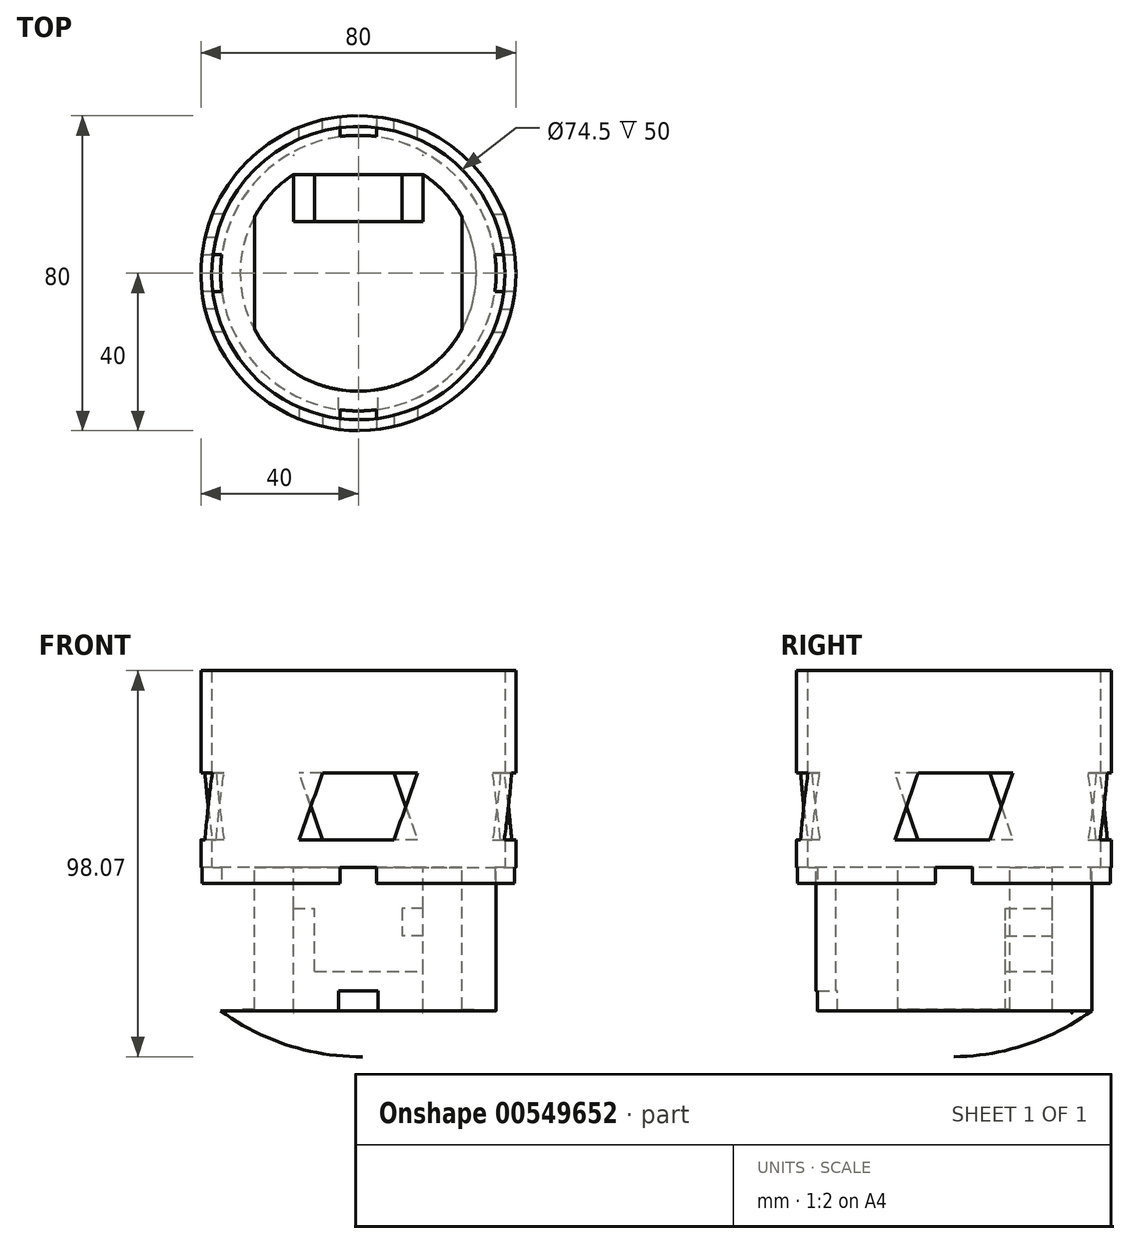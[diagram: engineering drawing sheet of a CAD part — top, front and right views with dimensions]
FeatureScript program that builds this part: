
annotation { "Feature Type Name" : "Feature", "Feature Type Description" : "" }
export const myFeature = defineFeature(function(context is Context, id is Id, definition is map)
    precondition{}
    {
        {
            var Q0;
            Q0=qCreatedBy(makeId("Top.planeOp"),FACE);
            var sketch = newSketch(context, id + "F0", { "sketchPlane" : qUnion([Q0])});
            skCircle(sketch, "E0", {"center": v(0, 0) * mm, "radius": 35 * mm});
            skCircle(sketch, "E1", {"center": v(0, 0) * mm, "radius": 30 * mm});
            skSolve(sketch);
        }
        {
            var Q0;
            Q0=makeQuery(id+"F0.imprint","IMPRINT",FACE,{"disambiguationData":[TD([[makeQuery(id+"F0.imprint","IMPRINT",EDGE,{"derivedFrom":sQuery(id+"F0.wireOp",EDGE,"E0")}),1.0]])]});
            extrude(context, id + "F1", {"entities" : qUnion([Q0]), "oppositeDirection" : true, "depth" : 10 * mm, "offsetDistance" : 25 * mm});
        }
        {
            var Q0;
            Q0=qCreatedBy(makeId("Top.planeOp"),FACE);
            var sketch = newSketch(context, id + "F2", { "sketchPlane" : qUnion([Q0])});
            skLineSegment(sketch, "E2.bottom", {"start": v(4.67, 54) * mm, "end": v(-4.68, 54) * mm});
            skLineSegment(sketch, "E2.top", {"start": v(4.68, 34) * mm, "end": v(-4.67, 34) * mm});
            skLineSegment(sketch, "E2.left", {"start": v(4.68, 54) * mm, "end": v(4.68, 34) * mm});
            skLineSegment(sketch, "E2.right", {"start": v(-4.67, 54) * mm, "end": v(-4.67, 34) * mm});
            skPoint(sketch, "E2.middle", {"position": v(0, 44) * mm});
            skSolve(sketch);
        }
        {
            var Q0;
            Q0=qSketchRegion(id+"F2",true);
            extrude(context, id + "F3", {"entities" : qUnion([Q0]), "operationType" : NewBodyOperationType.ADD, "oppositeDirection" : true, "depth" : 10 * mm, "offsetDistance" : 25 * mm});
        }
        {
            var Q0;
            Q0=qCreatedBy(makeId("Right.planeOp"),FACE);
            var sketch = newSketch(context, id + "F4", { "sketchPlane" : qUnion([Q0])});
            skLineSegment(sketch, "E3", {"start": v(0, 0) * mm, "end": v(0, -40) * mm});
            skSolve(sketch);
        }
        {
            var Q0;
            Q0=makeQuery(id+"F1.opExtrude","CAP_FACE",FACE,{"disambiguationData":[OSD([sQuery(id+"F0.wireOp",EDGE,"E0"),sQuery(id+"F0.wireOp",EDGE,"E1")])],"isStart":false});
            var sketch = newSketch(context, id + "F5", { "sketchPlane" : qUnion([Q0])});
            skCircle(sketch, "E4", {"center": v(0, 0) * mm, "radius": 30 * mm});
            skCircle(sketch, "E5", {"center": v(0, 0) * mm, "radius": 35 * mm});
            skSolve(sketch);
        }
        {
            var Q0;
            Q0=qSketchRegion(id+"F5",true);
            extrude(context, id + "F6", {"entities" : qUnion([Q0]), "depth" : 26.4 * mm, "offsetDistance" : 25 * mm});
        }
        {
            var Q0;
            Q0=qCreatedBy(makeId("Right.planeOp"),FACE);
            var sketch = newSketch(context, id + "F7", { "sketchPlane" : qUnion([Q0])});
            skLineSegment(sketch, "E6", {"start": v(0, 43.23) * mm, "end": v(0, 10.88) * mm});
            skSolve(sketch);
        }
        {
            var Q0;
            Q0=makeQuery(id+"F1.opExtrude","SWEPT_BODY",BODY,{"disambiguationData":[OSD([sQuery(id+"F0.wireOp",EDGE,"E0"),sQuery(id+"F0.wireOp",EDGE,"E1")])]});
            var Q1;
            Q1=sQuery(id+"F7.wireOp",EDGE,"E6");
            circularPattern(context, id + "F8", {"entities" : qUnion([Q0]), "axis" : qUnion([Q1]), "angle" : 360 * degree, "instanceCount" : 4, "equalSpace" : true});
        }
        {
            var Q0;
            Q0=qCreatedBy(makeId("Right.planeOp"),FACE);
            var sketch = newSketch(context, id + "F9", { "sketchPlane" : qUnion([Q0])});
            skLineSegment(sketch, "E7", {"start": v(0, -36.4) * mm, "end": v(0, -48.07) * mm});
            skLineSegment(sketch, "E8", {"start": v(0, -36.4) * mm, "end": v(-35, -36.4) * mm});
            skArc(sketch, "E9", {"start": v(-35, -36.4) * mm, "mid": v(-18.42, -44.99) * mm, "end": v(0, -48.07) * mm});
            skSolve(sketch);
        }
        {
            var Q0;
            Q0=qSketchRegion(id+"F9",true);
            var Q1;
            Q1=sQuery(id+"F7.wireOp",EDGE,"E6");
            revolve(context, id + "F10", {"operationType" : NewBodyOperationType.ADD, "entities" : qUnion([Q0]), "axis" : qUnion([Q1]), "revolveType" : RevolveType.FULL});
        }
        {
            var Q0;
            Q0=qCreatedBy(makeId("Top.planeOp"),FACE);
            var sketch = newSketch(context, id + "F11", { "sketchPlane" : qUnion([Q0])});
            skLineSegment(sketch, "E10.bottom", {"start": v(16.5, 25.05) * mm, "end": v(-16.5, 25.05) * mm});
            skLineSegment(sketch, "E10.top", {"start": v(16.5, 30) * mm, "end": v(-16.5, 30) * mm});
            skLineSegment(sketch, "E10.left", {"start": v(16.5, 25.05) * mm, "end": v(16.5, 30) * mm});
            skLineSegment(sketch, "E10.right", {"start": v(-16.5, 25.05) * mm, "end": v(-16.5, 30) * mm});
            skPoint(sketch, "E10.middle", {"position": v(0, 27.53) * mm});
            skSolve(sketch);
        }
        {
            var Q0;
            Q0=makeQuery(id+"F1.opExtrude","SWEPT_BODY",BODY,{"disambiguationData":[OSD([sQuery(id+"F0.wireOp",EDGE,"E0"),sQuery(id+"F0.wireOp",EDGE,"E1")])]});
            var Q1;
            Q1=makeQuery(id+"F6.opExtrude","SWEPT_BODY",BODY,{"disambiguationData":[OSD([sQuery(id+"F5.wireOp",EDGE,"E4"),sQuery(id+"F5.wireOp",EDGE,"E5")])]});
            var Q2;
            Q2=makeQuery(id+"F8.opPattern","COPY",BODY,{"derivedFrom":makeQuery(id+"F1.opExtrude","SWEPT_BODY",BODY,{"disambiguationData":[OSD([sQuery(id+"F0.wireOp",EDGE,"E0"),sQuery(id+"F0.wireOp",EDGE,"E1")])]}),"instanceName":"2"});
            var Q3;
            Q3=makeQuery(id+"F8.opPattern","COPY",BODY,{"derivedFrom":makeQuery(id+"F1.opExtrude","SWEPT_BODY",BODY,{"disambiguationData":[OSD([sQuery(id+"F0.wireOp",EDGE,"E0"),sQuery(id+"F0.wireOp",EDGE,"E1")])]}),"instanceName":"3"});
            var Q4;
            Q4=makeQuery(id+"F40aK8SqE4txYRV_3.opPattern","COPY",BODY,{"derivedFrom":makeQuery(id+"FKwpcLcn6bH6iQZ_2.opRevolve","SWEPT_BODY",BODY,{"disambiguationData":[OSD([sQuery(id+"FD4HdzIvPUUwVay_2.wireOp",EDGE,"a1goFWV3-hmGV-yWYP-BMxk-jAgMXw5Fhpe8"),sQuery(id+"FD4HdzIvPUUwVay_2.wireOp",EDGE,"Fw7PGfqN-QWwp-sSqB-PI52-uVMqbdzyiW2G"),sQuery(id+"FD4HdzIvPUUwVay_2.wireOp",EDGE,"nihQI9GH-8jKx-viQP-mQeq-4tLKAg00kZ77"),sQuery(id+"FD4HdzIvPUUwVay_2.wireOp",EDGE,"Pyl0iUsN-Orhq-JqrC-4vEJ-9OXzgTH1srMD")])]}),"instanceName":"1"});
            booleanBodies(context, id + "F12", {"operationType" : BooleanOperationType.UNION, "tools" : qUnion([Q0, Q1, Q2, Q3, Q4])});
        }
        {
            var Q0;
            Q0=makeQuery(id+"F1.opExtrude","SWEPT_BODY",BODY,{"disambiguationData":[OSD([sQuery(id+"F0.wireOp",EDGE,"E0"),sQuery(id+"F0.wireOp",EDGE,"E1")])]});
            var Q1;
            Q1=makeQuery(id+"F8.opPattern","COPY",BODY,{"derivedFrom":makeQuery(id+"F1.opExtrude","SWEPT_BODY",BODY,{"disambiguationData":[OSD([sQuery(id+"F0.wireOp",EDGE,"E0"),sQuery(id+"F0.wireOp",EDGE,"E1")])]}),"instanceName":"1"});
            var Q2;
            Q2=makeQuery(id+"FKwpcLcn6bH6iQZ_2.opRevolve","SWEPT_BODY",BODY,{"disambiguationData":[OSD([sQuery(id+"FD4HdzIvPUUwVay_2.wireOp",EDGE,"a1goFWV3-hmGV-yWYP-BMxk-jAgMXw5Fhpe8"),sQuery(id+"FD4HdzIvPUUwVay_2.wireOp",EDGE,"Fw7PGfqN-QWwp-sSqB-PI52-uVMqbdzyiW2G"),sQuery(id+"FD4HdzIvPUUwVay_2.wireOp",EDGE,"nihQI9GH-8jKx-viQP-mQeq-4tLKAg00kZ77"),sQuery(id+"FD4HdzIvPUUwVay_2.wireOp",EDGE,"Pyl0iUsN-Orhq-JqrC-4vEJ-9OXzgTH1srMD")])]});
            var Q3;
            Q3=makeQuery(id+"F40aK8SqE4txYRV_3.opPattern","COPY",BODY,{"derivedFrom":makeQuery(id+"FKwpcLcn6bH6iQZ_2.opRevolve","SWEPT_BODY",BODY,{"disambiguationData":[OSD([sQuery(id+"FD4HdzIvPUUwVay_2.wireOp",EDGE,"a1goFWV3-hmGV-yWYP-BMxk-jAgMXw5Fhpe8"),sQuery(id+"FD4HdzIvPUUwVay_2.wireOp",EDGE,"Fw7PGfqN-QWwp-sSqB-PI52-uVMqbdzyiW2G"),sQuery(id+"FD4HdzIvPUUwVay_2.wireOp",EDGE,"nihQI9GH-8jKx-viQP-mQeq-4tLKAg00kZ77"),sQuery(id+"FD4HdzIvPUUwVay_2.wireOp",EDGE,"Pyl0iUsN-Orhq-JqrC-4vEJ-9OXzgTH1srMD")])]}),"instanceName":"2"});
            var Q4;
            Q4=makeQuery(id+"F40aK8SqE4txYRV_3.opPattern","COPY",BODY,{"derivedFrom":makeQuery(id+"FKwpcLcn6bH6iQZ_2.opRevolve","SWEPT_BODY",BODY,{"disambiguationData":[OSD([sQuery(id+"FD4HdzIvPUUwVay_2.wireOp",EDGE,"a1goFWV3-hmGV-yWYP-BMxk-jAgMXw5Fhpe8"),sQuery(id+"FD4HdzIvPUUwVay_2.wireOp",EDGE,"Fw7PGfqN-QWwp-sSqB-PI52-uVMqbdzyiW2G"),sQuery(id+"FD4HdzIvPUUwVay_2.wireOp",EDGE,"nihQI9GH-8jKx-viQP-mQeq-4tLKAg00kZ77"),sQuery(id+"FD4HdzIvPUUwVay_2.wireOp",EDGE,"Pyl0iUsN-Orhq-JqrC-4vEJ-9OXzgTH1srMD")])]}),"instanceName":"3"});
            var Q5;
            Q5=makeQuery(id+"FgH07LaCN1YdpZV_3.opExtrude","SWEPT_BODY",BODY,{"disambiguationData":[OSD([sQuery(id+"FR34k6RjlDwe5vP_3.wireOp",EDGE,"LmRDcWpp-awj7-NGUQ-v67H-xGxEU0ThPCFp"),sQuery(id+"FR34k6RjlDwe5vP_3.wireOp",EDGE,"yXPaf9AL-SZNH-Mc4A-USQs-dOwJlW72xKXk"),sQuery(id+"FR34k6RjlDwe5vP_3.wireOp",EDGE,"sUruhic9-czyD-tmxL-6hvL-q4A46Xcr3Ddl"),sQuery(id+"FR34k6RjlDwe5vP_3.wireOp",EDGE,"kMsjgBrX-0vqh-hQ1Y-Rj0W-wmr9ZrnzLnDL")])]});
            var Q6;
            Q6=makeQuery(id+"FhvvMPg10EEFssR_4.opPattern","COPY",BODY,{"derivedFrom":makeQuery(id+"FgH07LaCN1YdpZV_3.opExtrude","SWEPT_BODY",BODY,{"disambiguationData":[OSD([sQuery(id+"FR34k6RjlDwe5vP_3.wireOp",EDGE,"LmRDcWpp-awj7-NGUQ-v67H-xGxEU0ThPCFp"),sQuery(id+"FR34k6RjlDwe5vP_3.wireOp",EDGE,"yXPaf9AL-SZNH-Mc4A-USQs-dOwJlW72xKXk"),sQuery(id+"FR34k6RjlDwe5vP_3.wireOp",EDGE,"sUruhic9-czyD-tmxL-6hvL-q4A46Xcr3Ddl"),sQuery(id+"FR34k6RjlDwe5vP_3.wireOp",EDGE,"kMsjgBrX-0vqh-hQ1Y-Rj0W-wmr9ZrnzLnDL")])]}),"instanceName":"1"});
            var Q7;
            Q7=makeQuery(id+"F8pSuF8Lx7vEzgG_4.opExtrude","SWEPT_BODY",BODY,{"disambiguationData":[OSD([sQuery(id+"F11.wireOp",EDGE,"E10.bottom"),sQuery(id+"F11.wireOp",EDGE,"E10.top"),sQuery(id+"F11.wireOp",EDGE,"E10.left"),sQuery(id+"F11.wireOp",EDGE,"E10.right")])]});
            var Q8;
            Q8=makeQuery(id+"FjD0aHrHDqX2kuE_5.opExtrude","SWEPT_BODY",BODY,{"disambiguationData":[OSD([sQuery(id+"FjwMsoveauJ2MpE_5.wireOp",EDGE,"X3daKeJd-6pMJ-jMlG-joWg-jZjprT1OWdNl.bottom"),sQuery(id+"FjwMsoveauJ2MpE_5.wireOp",EDGE,"X3daKeJd-6pMJ-jMlG-joWg-jZjprT1OWdNl.top"),sQuery(id+"FjwMsoveauJ2MpE_5.wireOp",EDGE,"X3daKeJd-6pMJ-jMlG-joWg-jZjprT1OWdNl.left"),sQuery(id+"FjwMsoveauJ2MpE_5.wireOp",EDGE,"X3daKeJd-6pMJ-jMlG-joWg-jZjprT1OWdNl.right")])]});
            var Q9;
            Q9=makeQuery(id+"FjD0aHrHDqX2kuE_5.opExtrude","SWEPT_BODY",BODY,{"disambiguationData":[OSD([sQuery(id+"FjwMsoveauJ2MpE_5.wireOp",EDGE,"aEOO42Y5-tFNn-AOk7-4746-zKCDvE4CHbXH.bottom"),sQuery(id+"FjwMsoveauJ2MpE_5.wireOp",EDGE,"aEOO42Y5-tFNn-AOk7-4746-zKCDvE4CHbXH.top"),sQuery(id+"FjwMsoveauJ2MpE_5.wireOp",EDGE,"aEOO42Y5-tFNn-AOk7-4746-zKCDvE4CHbXH.left"),sQuery(id+"FjwMsoveauJ2MpE_5.wireOp",EDGE,"aEOO42Y5-tFNn-AOk7-4746-zKCDvE4CHbXH.right"),sQuery(id+"FjwMsoveauJ2MpE_5.wireOp",EDGE,"ugEVnK5k-7QH2-G8G2-oESj-ZDwBd6VaRQGP.top"),sQuery(id+"FjwMsoveauJ2MpE_5.wireOp",EDGE,"ugEVnK5k-7QH2-G8G2-oESj-ZDwBd6VaRQGP.left"),sQuery(id+"FjwMsoveauJ2MpE_5.wireOp",EDGE,"ugEVnK5k-7QH2-G8G2-oESj-ZDwBd6VaRQGP.right")])]});
            booleanBodies(context, id + "F13", {"operationType" : BooleanOperationType.UNION, "tools" : qUnion([Q0, Q1, Q2, Q3, Q4, Q5, Q6, Q7, Q8, Q9])});
        }
        {
            var Q0;
            Q0=qSketchRegion(id+"F11",true);
            extrude(context, id + "F14", {"entities" : qUnion([Q0]), "operationType" : NewBodyOperationType.ADD, "oppositeDirection" : true, "depth" : 37 * mm, "offsetDistance" : 25 * mm});
        }
        {
            var Q0;
            Q0=makeQuery(id+"F14.opExtrude","SWEPT_FACE",FACE,{"disambiguationData":[OSD([sQuery(id+"F11.wireOp",EDGE,"E10.bottom")])]});
            var sketch = newSketch(context, id + "F15", { "sketchPlane" : qUnion([Q0])});
            skLineSegment(sketch, "E11.bottom", {"start": v(-16.5, -36.4) * mm, "end": v(16.5, -36.4) * mm});
            skLineSegment(sketch, "E11.top", {"start": v(-16.5, -26.4) * mm, "end": v(16.5, -26.4) * mm});
            skLineSegment(sketch, "E11.left", {"start": v(-16.5, -36.4) * mm, "end": v(-16.5, -26.4) * mm});
            skLineSegment(sketch, "E11.right", {"start": v(16.5, -36.4) * mm, "end": v(16.5, -26.4) * mm});
            skLineSegment(sketch, "E12.bottom", {"start": v(-16.5, -26.4) * mm, "end": v(-11.1, -26.4) * mm});
            skLineSegment(sketch, "E12.top", {"start": v(-16.5, -10.4) * mm, "end": v(-11.1, -10.4) * mm});
            skLineSegment(sketch, "E12.left", {"start": v(-16.5, -26.4) * mm, "end": v(-16.5, -10.4) * mm});
            skLineSegment(sketch, "E12.right", {"start": v(-11.1, -26.4) * mm, "end": v(-11.1, -10.4) * mm});
            skLineSegment(sketch, "E13.bottom", {"start": v(16.5, -10.4) * mm, "end": v(11.1, -10.4) * mm});
            skLineSegment(sketch, "E13.top", {"start": v(16.5, -17.4) * mm, "end": v(11.1, -17.4) * mm});
            skLineSegment(sketch, "E13.left", {"start": v(16.5, -10.4) * mm, "end": v(16.5, -17.4) * mm});
            skLineSegment(sketch, "E13.right", {"start": v(11.1, -10.4) * mm, "end": v(11.1, -17.4) * mm});
            skSolve(sketch);
        }
        {
            var Q0;
            Q0=qSketchRegion(id+"F15",true);
            extrude(context, id + "F16", {"entities" : qUnion([Q0]), "operationType" : NewBodyOperationType.ADD, "depth" : 12 * mm, "offsetDistance" : 25 * mm});
        }
        {
            var Q0;
            {var subQ0=makeQuery(id+"F3.boolean.opBoolean","MERGE",FACE,{"derivedFrom":[makeQuery(id+"F1.opExtrude","CAP_FACE",FACE,{"disambiguationData":[OSD([sQuery(id+"F0.wireOp",EDGE,"E0"),sQuery(id+"F0.wireOp",EDGE,"E1")])],"isStart":true}),makeQuery(id+"F3.opExtrude","CAP_FACE",FACE,{"disambiguationData":[OSD([sQuery(id+"F2.wireOp",EDGE,"E2.bottom"),sQuery(id+"F2.wireOp",EDGE,"E2.top"),sQuery(id+"F2.wireOp",EDGE,"E2.left"),sQuery(id+"F2.wireOp",EDGE,"E2.right")])],"isStart":true})]});Q0=makeQuery(id+"F14.boolean.opBoolean","MERGE",FACE,{"derivedFrom":[makeQuery(id+"F13.opBoolean","MERGE",FACE,{"derivedFrom":[makeQuery(id+"F8.opPattern","COPY",FACE,{"derivedFrom":subQ0,"instanceName":"1"}),makeQuery(id+"F12.opBoolean","MERGE",FACE,{"derivedFrom":[subQ0,makeQuery(id+"F8.opPattern","COPY",FACE,{"derivedFrom":subQ0,"instanceName":"2"}),makeQuery(id+"F8.opPattern","COPY",FACE,{"derivedFrom":subQ0,"instanceName":"3"})]})]}),makeQuery(id+"F14.opExtrude","CAP_FACE",FACE,{"disambiguationData":[OSD([sQuery(id+"F11.wireOp",EDGE,"E10.bottom"),sQuery(id+"F11.wireOp",EDGE,"E10.top"),sQuery(id+"F11.wireOp",EDGE,"E10.left"),sQuery(id+"F11.wireOp",EDGE,"E10.right")])],"isStart":true})]});}
            var sketch = newSketch(context, id + "F17", { "sketchPlane" : qUnion([Q0])});
            skLineSegment(sketch, "E14.bottom", {"start": v(-31.49, 14.23) * mm, "end": v(-26.4, 14.23) * mm});
            skLineSegment(sketch, "E14.top", {"start": v(-31.49, -14.23) * mm, "end": v(-26.4, -14.23) * mm});
            skLineSegment(sketch, "E14.left", {"start": v(-31.49, 14.23) * mm, "end": v(-31.49, -14.23) * mm});
            skLineSegment(sketch, "E14.right", {"start": v(-26.4, 14.23) * mm, "end": v(-26.4, -14.23) * mm});
            skLineSegment(sketch, "E15", {"start": v(0, 0) * mm, "end": v(0, -11.57) * mm, "construction": true});
            skLineSegment(sketch, "E16.MirrorCS", {"start": v(26.4, 14.23) * mm, "end": v(26.4, -14.23) * mm});
            skLineSegment(sketch, "E17.MirrorCS", {"start": v(31.49, 14.23) * mm, "end": v(31.49, -14.23) * mm});
            skLineSegment(sketch, "E18.MirrorCS", {"start": v(31.49, 14.23) * mm, "end": v(26.4, 14.23) * mm});
            skLineSegment(sketch, "E19.MirrorCS", {"start": v(31.49, -14.23) * mm, "end": v(26.4, -14.23) * mm});
            skSolve(sketch);
        }
        {
            var Q0;
            Q0=qSketchRegion(id+"F17",true);
            extrude(context, id + "F18", {"entities" : qUnion([Q0]), "operationType" : NewBodyOperationType.ADD, "oppositeDirection" : true, "depth" : 36 * mm, "offsetDistance" : 25 * mm});
        }
        {
            var Q0;
            Q0=makeQuery(id+"F16.opExtrude","CAP_FACE",FACE,{"disambiguationData":[OSD([sQuery(id+"F15.wireOp",EDGE,"E11.bottom"),sQuery(id+"F15.wireOp",EDGE,"E11.top"),sQuery(id+"F15.wireOp",EDGE,"E11.left"),sQuery(id+"F15.wireOp",EDGE,"E11.right"),sQuery(id+"F15.wireOp",EDGE,"E12.top"),sQuery(id+"F15.wireOp",EDGE,"E12.left"),sQuery(id+"F15.wireOp",EDGE,"E12.right")])],"isStart":false});
            var sketch = newSketch(context, id + "F19", { "sketchPlane" : qUnion([Q0])});
            skLineSegment(sketch, "E20.bottom", {"start": v(5, -36.4) * mm, "end": v(-5, -36.4) * mm});
            skLineSegment(sketch, "E20.top", {"start": v(5, -31.4) * mm, "end": v(-5, -31.4) * mm});
            skLineSegment(sketch, "E20.left", {"start": v(5, -36.4) * mm, "end": v(5, -31.4) * mm});
            skLineSegment(sketch, "E20.right", {"start": v(-5, -36.4) * mm, "end": v(-5, -31.4) * mm});
            skPoint(sketch, "E20.middle", {"position": v(0, -33.9) * mm});
            skSolve(sketch);
        }
        {
            var Q0;
            Q0=qSketchRegion(id+"F19",true);
            extrude(context, id + "F20", {"entities" : qUnion([Q0]), "operationType" : NewBodyOperationType.REMOVE, "depth" : 54.2 * mm, "offsetDistance" : 25 * mm});
        }
        {
            var Q0;
            {var subQ0=makeQuery(id+"F3.boolean.opBoolean","MERGE",FACE,{"derivedFrom":[makeQuery(id+"F1.opExtrude","CAP_FACE",FACE,{"disambiguationData":[OSD([sQuery(id+"F0.wireOp",EDGE,"E0"),sQuery(id+"F0.wireOp",EDGE,"E1")])],"isStart":true}),makeQuery(id+"F3.opExtrude","CAP_FACE",FACE,{"disambiguationData":[OSD([sQuery(id+"F2.wireOp",EDGE,"E2.bottom"),sQuery(id+"F2.wireOp",EDGE,"E2.top"),sQuery(id+"F2.wireOp",EDGE,"E2.left"),sQuery(id+"F2.wireOp",EDGE,"E2.right")])],"isStart":true})]});Q0=makeQuery(id+"F18.boolean.opBoolean","MERGE",FACE,{"derivedFrom":[makeQuery(id+"F14.boolean.opBoolean","MERGE",FACE,{"derivedFrom":[makeQuery(id+"F13.opBoolean","MERGE",FACE,{"derivedFrom":[makeQuery(id+"F8.opPattern","COPY",FACE,{"derivedFrom":subQ0,"instanceName":"1"}),makeQuery(id+"F12.opBoolean","MERGE",FACE,{"derivedFrom":[subQ0,makeQuery(id+"F8.opPattern","COPY",FACE,{"derivedFrom":subQ0,"instanceName":"2"}),makeQuery(id+"F8.opPattern","COPY",FACE,{"derivedFrom":subQ0,"instanceName":"3"})]})]}),makeQuery(id+"F14.opExtrude","CAP_FACE",FACE,{"disambiguationData":[OSD([sQuery(id+"F11.wireOp",EDGE,"E10.bottom"),sQuery(id+"F11.wireOp",EDGE,"E10.top"),sQuery(id+"F11.wireOp",EDGE,"E10.left"),sQuery(id+"F11.wireOp",EDGE,"E10.right")])],"isStart":true})]}),makeQuery(id+"F18.opExtrude","CAP_FACE",FACE,{"disambiguationData":[OSD([sQuery(id+"F17.wireOp",EDGE,"E14.bottom"),sQuery(id+"F17.wireOp",EDGE,"E14.top"),sQuery(id+"F17.wireOp",EDGE,"E14.left"),sQuery(id+"F17.wireOp",EDGE,"E14.right")])],"isStart":true}),makeQuery(id+"F18.opExtrude","CAP_FACE",FACE,{"disambiguationData":[OSD([sQuery(id+"F17.wireOp",EDGE,"E16.MirrorCS"),sQuery(id+"F17.wireOp",EDGE,"E17.MirrorCS"),sQuery(id+"F17.wireOp",EDGE,"E18.MirrorCS"),sQuery(id+"F17.wireOp",EDGE,"E19.MirrorCS")])],"isStart":true})]});}
            var sketch = newSketch(context, id + "F21", { "sketchPlane" : qUnion([Q0])});
            skCircle(sketch, "E21", {"center": v(0, 0) * mm, "radius": 40 * mm});
            skCircle(sketch, "E22", {"center": v(0, 0) * mm, "radius": 37.25 * mm});
            skSolve(sketch);
        }
        {
            var Q0;
            Q0=qSketchRegion(id+"F21",true);
            extrude(context, id + "F22", {"entities" : qUnion([Q0]), "operationType" : NewBodyOperationType.ADD, "depth" : 50 * mm, "offsetDistance" : 25 * mm});
        }
        {
            var Q0;
            {var subQ0=sQuery(id+"F0.wireOp",EDGE,"E0");var subQ1=makeQuery(id+"F1.opExtrude","SWEPT_FACE",FACE,{"disambiguationData":[OSD([subQ0])]});var subQ2=sQuery(id+"F0.wireOp",EDGE,"E1");var subQ4=sQuery(id+"F2.wireOp",EDGE,"E2.right");var subQ6=sQuery(id+"F2.wireOp",EDGE,"E2.left");var subQ10=sQuery(id+"F11.wireOp",EDGE,"E10.bottom");var subQ11=sQuery(id+"F17.wireOp",EDGE,"E14.right");var subQ12=sQuery(id+"F17.wireOp",EDGE,"E16.MirrorCS");var subQ14=makeQuery(id+"F3.boolean.opBoolean","MERGE",FACE,{"derivedFrom":[makeQuery(id+"F1.opExtrude","CAP_FACE",FACE,{"disambiguationData":[OSD([subQ0,subQ2])],"isStart":true}),makeQuery(id+"F3.opExtrude","CAP_FACE",FACE,{"disambiguationData":[OSD([sQuery(id+"F2.wireOp",EDGE,"E2.bottom"),sQuery(id+"F2.wireOp",EDGE,"E2.top"),subQ6,subQ4])],"isStart":true})]});Q0=makeQuery(id+"F22.boolean.opBoolean","SPLIT",FACE,{"disambiguationData":[TD([subQ1])],"derivedFrom":makeQuery(id+"F18.boolean.opBoolean","MERGE",FACE,{"derivedFrom":[makeQuery(id+"F14.boolean.opBoolean","MERGE",FACE,{"derivedFrom":[makeQuery(id+"F13.opBoolean","MERGE",FACE,{"derivedFrom":[makeQuery(id+"F8.opPattern","COPY",FACE,{"derivedFrom":subQ14,"instanceName":"1"}),makeQuery(id+"F12.opBoolean","MERGE",FACE,{"derivedFrom":[subQ14,makeQuery(id+"F8.opPattern","COPY",FACE,{"derivedFrom":subQ14,"instanceName":"2"}),makeQuery(id+"F8.opPattern","COPY",FACE,{"derivedFrom":subQ14,"instanceName":"3"})]})]}),makeQuery(id+"F14.opExtrude","CAP_FACE",FACE,{"disambiguationData":[OSD([subQ10,sQuery(id+"F11.wireOp",EDGE,"E10.top"),sQuery(id+"F11.wireOp",EDGE,"E10.left"),sQuery(id+"F11.wireOp",EDGE,"E10.right")])],"isStart":true})]}),makeQuery(id+"F18.opExtrude","CAP_FACE",FACE,{"disambiguationData":[OSD([sQuery(id+"F17.wireOp",EDGE,"E14.bottom"),sQuery(id+"F17.wireOp",EDGE,"E14.top"),sQuery(id+"F17.wireOp",EDGE,"E14.left"),subQ11])],"isStart":true}),makeQuery(id+"F18.opExtrude","CAP_FACE",FACE,{"disambiguationData":[OSD([subQ12,sQuery(id+"F17.wireOp",EDGE,"E17.MirrorCS"),sQuery(id+"F17.wireOp",EDGE,"E18.MirrorCS"),sQuery(id+"F17.wireOp",EDGE,"E19.MirrorCS")])],"isStart":true})]})});}
            var sketch = newSketch(context, id + "F23", { "sketchPlane" : qUnion([Q0])});
            skCircle(sketch, "E23", {"center": v(0, 0) * mm, "radius": 40 * mm});
            skCircle(sketch, "E24", {"center": v(0, 0) * mm, "radius": 34.39 * mm});
            skSolve(sketch);
        }
        {
            var Q0;
            Q0=qSketchRegion(id+"F23",true);
            extrude(context, id + "F24", {"entities" : qUnion([Q0]), "operationType" : NewBodyOperationType.ADD, "oppositeDirection" : true, "depth" : 4 * mm, "offsetDistance" : 25 * mm});
        }
        {
            var Q0;
            Q0=qCreatedBy(makeId("Front.planeOp"),FACE);
            cPlane(context, id + "F25", {"entities" : qUnion([Q0]), "cplaneType" : CPlaneType.OFFSET, "offset" : 44 * mm, "width" : 150 * mm, "height" : 150 * mm});
        }
        {
            var Q0;
            Q0=qCreatedBy(makeId("Front.planeOp"),FACE);
            cPlane(context, id + "F26", {"entities" : qUnion([Q0]), "cplaneType" : CPlaneType.OFFSET, "offset" : 44 * mm, "oppositeDirection" : true, "width" : 150 * mm, "height" : 150 * mm});
        }
        {
            var Q0;
            Q0=qCreatedBy(makeId("Right.planeOp"),FACE);
            cPlane(context, id + "F27", {"entities" : qUnion([Q0]), "cplaneType" : CPlaneType.OFFSET, "offset" : 44 * mm, "width" : 150 * mm, "height" : 150 * mm});
        }
        {
            var Q0;
            Q0=qCreatedBy(makeId("Right.planeOp"),FACE);
            cPlane(context, id + "F28", {"entities" : qUnion([Q0]), "cplaneType" : CPlaneType.OFFSET, "offset" : 44 * mm, "oppositeDirection" : true, "width" : 150 * mm, "height" : 150 * mm});
        }
        {
            var Q0;
            Q0=qCreatedBy(id+"F25.planeOp",FACE);
            var sketch = newSketch(context, id + "F29", { "sketchPlane" : qUnion([Q0])});
            skLineSegment(sketch, "E25.bottom", {"start": v(15, 24) * mm, "end": v(-9.08, 24) * mm});
            skLineSegment(sketch, "E25.top", {"start": v(9.08, 7) * mm, "end": v(-15, 7) * mm});
            skPoint(sketch, "E25.middle", {"position": v(0, 15.5) * mm});
            skLineSegment(sketch, "E26", {"start": v(-15, 7) * mm, "end": v(-9.08, 24) * mm});
            skLineSegment(sketch, "E27", {"start": v(15, 24) * mm, "end": v(9.08, 7) * mm});
            skPoint(sketch, "E28.orphan", {"position": v(-15, 24) * mm});
            skPoint(sketch, "E29.orphan", {"position": v(15, 7) * mm});
            skSolve(sketch);
        }
        {
            var Q0;
            Q0=qSketchRegion(id+"F29",true);
            extrude(context, id + "F30", {"entities" : qUnion([Q0]), "operationType" : NewBodyOperationType.REMOVE, "oppositeDirection" : true, "depth" : 20.7 * mm, "offsetDistance" : 25 * mm});
        }
        {
            var Q0;
            Q0=qCreatedBy(id+"F26.planeOp",FACE);
            var sketch = newSketch(context, id + "F31", { "sketchPlane" : qUnion([Q0])});
            skLineSegment(sketch, "E30.bottom", {"start": v(-15, 24) * mm, "end": v(9.08, 24) * mm});
            skLineSegment(sketch, "E30.top", {"start": v(-9.08, 7) * mm, "end": v(15, 7) * mm});
            skPoint(sketch, "E30.middle", {"position": v(0, 15.5) * mm});
            skLineSegment(sketch, "E31", {"start": v(15, 7) * mm, "end": v(9.08, 24) * mm});
            skLineSegment(sketch, "E32", {"start": v(-15, 24) * mm, "end": v(-9.08, 7) * mm});
            skPoint(sketch, "E30.right.start.orphan", {"position": v(15, 24) * mm});
            skPoint(sketch, "E33.orphan", {"position": v(-15, 7) * mm});
            skSolve(sketch);
        }
        {
            var Q0;
            Q0=qSketchRegion(id+"F31",true);
            extrude(context, id + "F32", {"entities" : qUnion([Q0]), "operationType" : NewBodyOperationType.REMOVE, "depth" : 25 * mm, "offsetDistance" : 25 * mm});
        }
        {
            var Q0;
            Q0=qCreatedBy(id+"F27.planeOp",FACE);
            var sketch = newSketch(context, id + "F33", { "sketchPlane" : qUnion([Q0])});
            skLineSegment(sketch, "E34.bottom", {"start": v(15, 24) * mm, "end": v(-9.08, 24) * mm});
            skLineSegment(sketch, "E34.top", {"start": v(9.08, 7) * mm, "end": v(-15, 7) * mm});
            skPoint(sketch, "E34.middle", {"position": v(0, 15.5) * mm});
            skLineSegment(sketch, "E35", {"start": v(-15, 7) * mm, "end": v(-9.08, 24) * mm});
            skLineSegment(sketch, "E36", {"start": v(15, 24) * mm, "end": v(9.08, 7) * mm});
            skPoint(sketch, "E34.right.start.orphan", {"position": v(-15, 24) * mm});
            skPoint(sketch, "E34.left.end.orphan", {"position": v(15, 7) * mm});
            skSolve(sketch);
        }
        {
            var Q0;
            Q0=qSketchRegion(id+"F33",true);
            extrude(context, id + "F34", {"entities" : qUnion([Q0]), "operationType" : NewBodyOperationType.REMOVE, "oppositeDirection" : true, "depth" : 25 * mm, "offsetDistance" : 25 * mm});
        }
        {
            var Q0;
            Q0=qCreatedBy(id+"F28.planeOp",FACE);
            var sketch = newSketch(context, id + "F35", { "sketchPlane" : qUnion([Q0])});
            skLineSegment(sketch, "E37.bottom", {"start": v(-15, 24) * mm, "end": v(9.08, 24) * mm});
            skLineSegment(sketch, "E37.top", {"start": v(-9.08, 7) * mm, "end": v(15, 7) * mm});
            skPoint(sketch, "E37.middle", {"position": v(0, 15.5) * mm});
            skLineSegment(sketch, "E38", {"start": v(15, 7) * mm, "end": v(9.08, 24) * mm});
            skLineSegment(sketch, "E39", {"start": v(-15, 24) * mm, "end": v(-9.08, 7) * mm});
            skPoint(sketch, "E37.right.start.orphan", {"position": v(15, 24) * mm});
            skPoint(sketch, "E37.left.end.orphan", {"position": v(-15, 7) * mm});
            skSolve(sketch);
        }
        {
            var Q0;
            Q0=qSketchRegion(id+"F35",true);
            extrude(context, id + "F36", {"entities" : qUnion([Q0]), "operationType" : NewBodyOperationType.REMOVE, "depth" : 25 * mm, "offsetDistance" : 25 * mm});
        }
        {
            var Q0;
            Q0=makeQuery(id+"F3.boolean.opBoolean","MERGE",FACE,{"derivedFrom":[makeQuery(id+"F1.opExtrude","CAP_FACE",FACE,{"disambiguationData":[OSD([sQuery(id+"F0.wireOp",EDGE,"E0"),sQuery(id+"F0.wireOp",EDGE,"E1")])],"isStart":false}),makeQuery(id+"F3.opExtrude","CAP_FACE",FACE,{"disambiguationData":[OSD([sQuery(id+"F2.wireOp",EDGE,"E2.bottom"),sQuery(id+"F2.wireOp",EDGE,"E2.top"),sQuery(id+"F2.wireOp",EDGE,"E2.left"),sQuery(id+"F2.wireOp",EDGE,"E2.right")])],"isStart":false})]});
            var sketch = newSketch(context, id + "F37", { "sketchPlane" : qUnion([Q0])});
            skArc(sketch, "E40", {"start": v(-4.68, -34.69) * mm, "mid": v(0, -35) * mm, "end": v(4.68, -34.69) * mm});
            skLineSegment(sketch, "E41", {"start": v(-4.67, -34.69) * mm, "end": v(-4.68, -54) * mm});
            skLineSegment(sketch, "E42", {"start": v(-4.68, -54) * mm, "end": v(4.67, -54) * mm});
            skLineSegment(sketch, "E43", {"start": v(4.68, -54) * mm, "end": v(4.68, -34.69) * mm});
            skLineSegment(sketch, "E44.1.0", {"start": v(54, 4.67) * mm, "end": v(34.69, 4.68) * mm});
            skLineSegment(sketch, "E44.1.1", {"start": v(34.69, -4.68) * mm, "end": v(54, -4.68) * mm});
            skArc(sketch, "E44.1.2", {"start": v(34.69, -4.68) * mm, "mid": v(35, 0) * mm, "end": v(34.69, 4.68) * mm});
            skLineSegment(sketch, "E44.1.3", {"start": v(54, -4.68) * mm, "end": v(54, 4.67) * mm});
            skLineSegment(sketch, "E44.2.0", {"start": v(-4.67, 54) * mm, "end": v(-4.68, 34.69) * mm});
            skLineSegment(sketch, "E44.2.1", {"start": v(4.68, 34.69) * mm, "end": v(4.68, 54) * mm});
            skArc(sketch, "E44.2.2", {"start": v(4.68, 34.69) * mm, "mid": v(0, 35) * mm, "end": v(-4.68, 34.69) * mm});
            skLineSegment(sketch, "E44.2.3", {"start": v(4.68, 54) * mm, "end": v(-4.67, 54) * mm});
            skLineSegment(sketch, "E44.3.0", {"start": v(-54, -4.67) * mm, "end": v(-34.69, -4.67) * mm});
            skLineSegment(sketch, "E44.3.1", {"start": v(-34.69, 4.68) * mm, "end": v(-54, 4.68) * mm});
            skArc(sketch, "E44.3.2", {"start": v(-34.69, 4.68) * mm, "mid": v(-35, 0) * mm, "end": v(-34.69, -4.68) * mm});
            skLineSegment(sketch, "E44.3.3", {"start": v(-54, 4.68) * mm, "end": v(-54, -4.67) * mm});
            skSolve(sketch);
        }
        {
            var Q0;
            Q0 = qSketchRegion(id + "F37", true);
            extrude(context, id + "F38", {"entities" : qUnion([Q0]), "operationType" : NewBodyOperationType.REMOVE, "oppositeDirection" : true, "depth" : 10 * mm, "offsetDistance" : 25 * mm});
        }
    });
